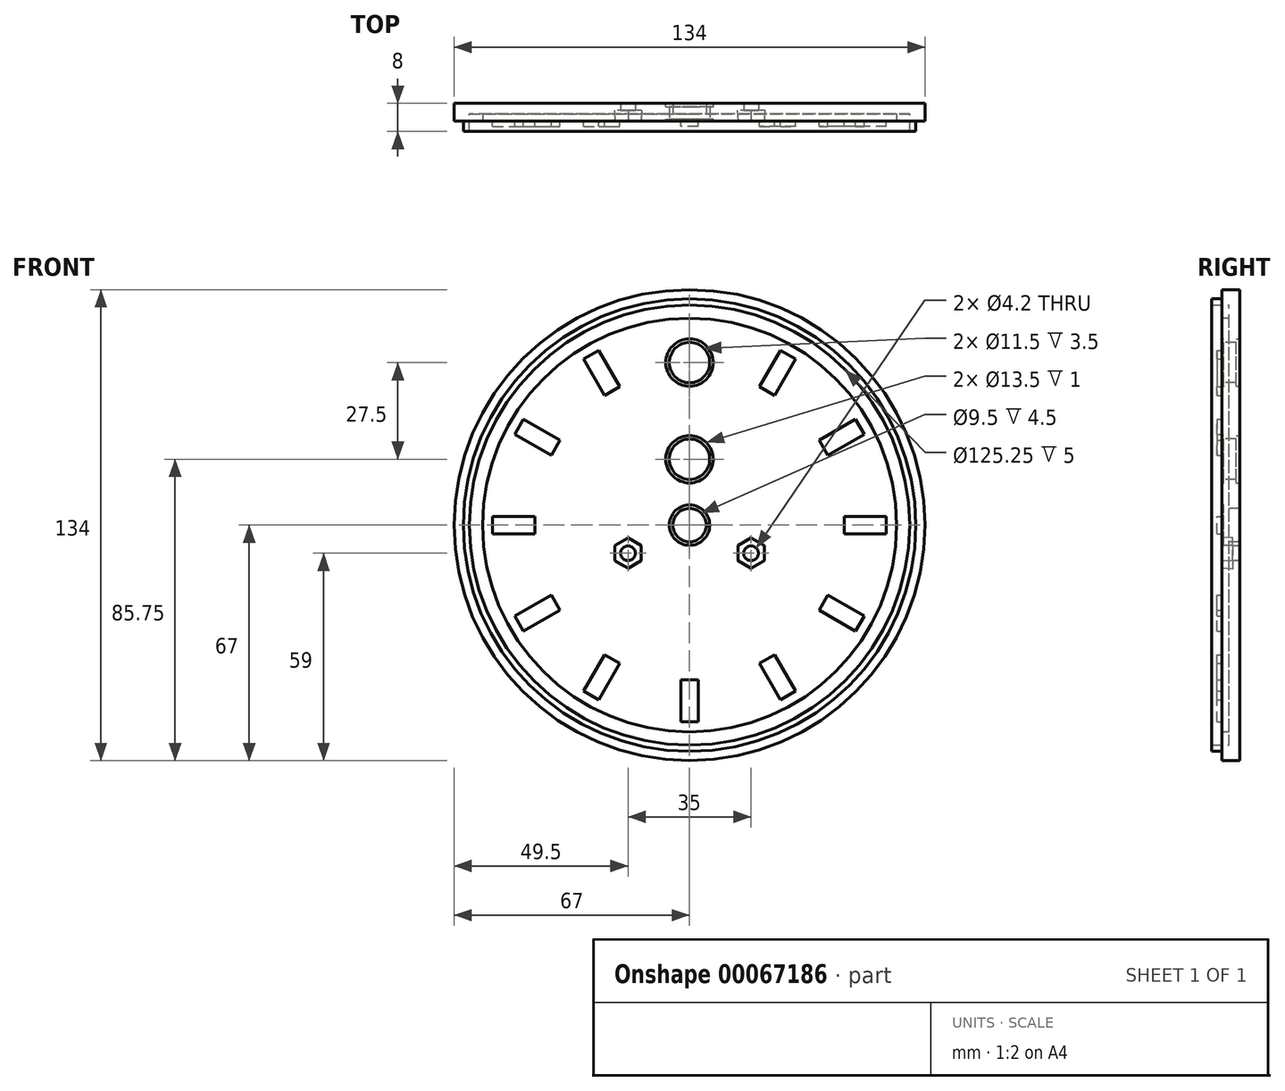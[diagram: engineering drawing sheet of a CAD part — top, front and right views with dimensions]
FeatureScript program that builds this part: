
annotation { "Feature Type Name" : "Feature", "Feature Type Description" : "" }
export const myFeature = defineFeature(function(context is Context, id is Id, definition is map)
    precondition{}
    {
        {
            var Q0;
            Q0=qCreatedBy(makeId("Front.planeOp"),FACE);
            var sketch = newSketch(context, id + "F0", { "sketchPlane" : qUnion([Q0])});
            skCircle(sketch, "E0", {"center": v(0, 0) * mm, "radius": 67 * mm});
            skSolve(sketch);
        }
        {
            var Q0;
            Q0 = qSketchRegion(id + "F0", true);
            extrude(context, id + "F1", {"entities" : qUnion([Q0]), "depth" : 5 * mm});
        }
        {
            var Q0;
            Q0=makeQuery(id+"F1.opExtrude","CAP_FACE",FACE,{"disambiguationData":[OSD([sQuery(id+"F0.wireOp",EDGE,"E0")])],"isStart":false});
            var sketch = newSketch(context, id + "F2", { "sketchPlane" : qUnion([Q0])});
            skCircle(sketch, "E1", {"center": v(0, 0) * mm, "radius": 58.88 * mm});
            skCircle(sketch, "E2", {"center": v(0, 0) * mm, "radius": 62.62 * mm});
            skCircle(sketch, "E3", {"center": v(0, 0) * mm, "radius": 64.38 * mm});
            skSolve(sketch);
        }
        {
            var Q0;
            Q0=makeQuery(id+"F2.imprint","IMPRINT",FACE,{"disambiguationData":[TD([[makeQuery(id+"F2.imprint","IMPRINT",EDGE,{"derivedFrom":sQuery(id+"F2.wireOp",EDGE,"E2")}),-1.0]])]});
            extrude(context, id + "F3", {"entities" : qUnion([Q0]), "operationType" : NewBodyOperationType.ADD, "depth" : 3 * mm});
        }
        {
            var Q0;
            Q0=makeQuery(id+"F2.imprint","IMPRINT",FACE,{"disambiguationData":[TD([[makeQuery(id+"F2.imprint","IMPRINT",EDGE,{"derivedFrom":sQuery(id+"F2.wireOp",EDGE,"E1")}),-1.0]])]});
            extrude(context, id + "F4", {"entities" : qUnion([Q0]), "operationType" : NewBodyOperationType.REMOVE, "oppositeDirection" : true, "depth" : 2 * mm});
        }
        {
            var Q0;
            Q0=makeQuery(id+"F2.imprint","IMPRINT",FACE,{"disambiguationData":[TD([[makeQuery(id+"F2.imprint","IMPRINT",EDGE,{"derivedFrom":sQuery(id+"F2.wireOp",EDGE,"E1")}),1.0]])]});
            var sketch = newSketch(context, id + "F5", { "sketchPlane" : qUnion([Q0])});
            skCircle(sketch, "E4", {"center": v(0, 0) * mm, "radius": 4.75 * mm});
            skLineSegment(sketch, "E5", {"start": v(0, 0) * mm, "end": v(0, 18.75) * mm, "construction": true});
            skCircle(sketch, "E6", {"center": v(0, 18.75) * mm, "radius": 5.75 * mm});
            skLineSegment(sketch, "E7", {"start": v(0, 18.75) * mm, "end": v(0, 46.25) * mm, "construction": true});
            skCircle(sketch, "E8", {"center": v(0, 46.25) * mm, "radius": 5.75 * mm});
            skLineSegment(sketch, "E9", {"start": v(0, 0) * mm, "end": v(0, -8) * mm, "construction": true});
            skLineSegment(sketch, "E10", {"start": v(0, -8) * mm, "end": v(17.5, -8) * mm, "construction": true});
            skCircle(sketch, "E11", {"center": v(17.5, -8) * mm, "radius": 2.1 * mm});
            skCircle(sketch, "E12.MirrorC", {"center": v(-17.5, -8) * mm, "radius": 2.1 * mm});
            skSolve(sketch);
        }
        {
            var Q0;
            Q0 = qSketchRegion(id + "F5", true);
            extrude(context, id + "F6", {"entities" : qUnion([Q0]), "operationType" : NewBodyOperationType.REMOVE, "oppositeDirection" : true, "depth" : 25 * mm});
        }
        {
            var Q0;
            Q0=makeQuery(id+"F2.imprint","IMPRINT",FACE,{"disambiguationData":[TD([[makeQuery(id+"F2.imprint","IMPRINT",EDGE,{"derivedFrom":sQuery(id+"F2.wireOp",EDGE,"E1")}),1.0]])]});
            var sketch = newSketch(context, id + "F7", { "sketchPlane" : qUnion([Q0])});
            skCircle(sketch, "E13", {"center": v(0, 0) * mm, "radius": 5.75 * mm});
            skCircle(sketch, "E14", {"center": v(0, 18.75) * mm, "radius": 6.75 * mm});
            skCircle(sketch, "E15", {"center": v(0, 46.25) * mm, "radius": 6.75 * mm});
            skSolve(sketch);
        }
        {
            var Q0;
            Q0 = qSketchRegion(id + "F7", true);
            extrude(context, id + "F8", {"entities" : qUnion([Q0]), "operationType" : NewBodyOperationType.REMOVE, "oppositeDirection" : true, "depth" : .5 * mm, "hasDraft" : true, "draftAngle" : 3 * degree});
        }
        {
            var Q0;
            Q0=makeQuery(id+"F2.imprint","IMPRINT",FACE,{"disambiguationData":[TD([[makeQuery(id+"F2.imprint","IMPRINT",EDGE,{"derivedFrom":sQuery(id+"F2.wireOp",EDGE,"E1")}),1.0]])]});
            var sketch = newSketch(context, id + "F9", { "sketchPlane" : qUnion([Q0])});
            skCircle(sketch, "E16.cCircle", {"center": v(17.5, -8) * mm, "radius": 3.75 * mm, "construction": true});
            skLineSegment(sketch, "E16.0", {"start": v(21.25, -5.83) * mm, "end": v(21.25, -10.17) * mm});
            skLineSegment(sketch, "E16.1", {"start": v(21.25, -10.17) * mm, "end": v(17.5, -12.33) * mm});
            skLineSegment(sketch, "E16.2", {"start": v(17.5, -12.33) * mm, "end": v(13.75, -10.17) * mm});
            skLineSegment(sketch, "E16.3", {"start": v(13.75, -10.17) * mm, "end": v(13.75, -5.83) * mm});
            skLineSegment(sketch, "E16.4", {"start": v(13.75, -5.83) * mm, "end": v(17.5, -3.67) * mm});
            skLineSegment(sketch, "E16.5", {"start": v(17.5, -3.67) * mm, "end": v(21.25, -5.83) * mm});
            skPoint(sketch, "E16.0.midPoint", {"position": v(21.25, -8) * mm});
            skLineSegment(sketch, "E17.MirrorCS", {"start": v(-21.25, -5.83) * mm, "end": v(-21.25, -10.17) * mm});
            skLineSegment(sketch, "E18.MirrorCS", {"start": v(-13.75, -5.83) * mm, "end": v(-17.5, -3.67) * mm});
            skLineSegment(sketch, "E19.MirrorCS", {"start": v(-17.5, -3.67) * mm, "end": v(-21.25, -5.83) * mm});
            skCircle(sketch, "E20.MirrorC", {"center": v(-17.5, -8) * mm, "radius": 3.75 * mm, "construction": true});
            skPoint(sketch, "E21.MirrorP", {"position": v(-21.25, -8) * mm});
            skLineSegment(sketch, "E22.MirrorCS", {"start": v(-21.25, -10.17) * mm, "end": v(-17.5, -12.33) * mm});
            skLineSegment(sketch, "E23.MirrorCS", {"start": v(-17.5, -12.33) * mm, "end": v(-13.75, -10.17) * mm});
            skLineSegment(sketch, "E24.MirrorCS", {"start": v(-13.75, -10.17) * mm, "end": v(-13.75, -5.83) * mm});
            skSolve(sketch);
        }
        {
            var Q0;
            Q0 = qSketchRegion(id + "F9", true);
            extrude(context, id + "F10", {"entities" : qUnion([Q0]), "operationType" : NewBodyOperationType.REMOVE, "oppositeDirection" : true, "depth" : 3 * mm, "hasDraft" : true, "draftAngle" : 3 * degree});
        }
        {
            var Q0;
            Q0=qCreatedBy(makeId("Front.planeOp"),FACE);
            var sketch = newSketch(context, id + "F11", { "sketchPlane" : qUnion([Q0])});
            skCircle(sketch, "E25.0", {"center": v(0, 46.25) * mm, "radius": 6.75 * mm});
            skCircle(sketch, "E25.1", {"center": v(0, 18.75) * mm, "radius": 6.75 * mm});
            skSolve(sketch);
        }
        {
            var Q0;
            Q0 = qSketchRegion(id + "F11", true);
            extrude(context, id + "F12", {"entities" : qUnion([Q0]), "operationType" : NewBodyOperationType.REMOVE, "depth" : 1 * mm});
        }
        {
            var Q0;
            Q0=makeQuery(id+"F7.imprint","IMPRINT",FACE,{"disambiguationData":[TD([[makeQuery(id+"F7.imprint","IMPRINT",EDGE,{"derivedFrom":sQuery(id+"F7.wireOp",EDGE,"E13")}),-1.0]])]});
            var sketch = newSketch(context, id + "F13", { "sketchPlane" : qUnion([Q0])});
            skCircle(sketch, "E26", {"center": v(0, 0) * mm, "radius": 50 * mm, "construction": true});
            skPoint(sketch, "E27", {"position": v(0, -50) * mm});
            skLineSegment(sketch, "E28.rect.bottom", {"start": v(2.5, -56) * mm, "end": v(-2.5, -56) * mm});
            skLineSegment(sketch, "E28.rect.top", {"start": v(2.5, -44) * mm, "end": v(-2.5, -44) * mm});
            skLineSegment(sketch, "E28.rect.left", {"start": v(2.5, -56) * mm, "end": v(2.5, -44) * mm});
            skLineSegment(sketch, "E28.rect.right", {"start": v(-2.5, -56) * mm, "end": v(-2.5, -44) * mm});
            skLineSegment(sketch, "E29", {"start": v(0, -66.73) * mm, "end": v(0, 0) * mm, "construction": true});
            skSolve(sketch);
        }
        {
            var Q0;
            Q0 = qSketchRegion(id + "F13", true);
            extrude(context, id + "F14", {"entities" : qUnion([Q0]), "operationType" : NewBodyOperationType.ADD, "depth" : 1.5 * mm});
        }
        {
            var Q0;
            Q0=makeQuery(id+"F14.opExtrude","SWEPT_FACE",FACE,{"disambiguationData":[OSD([sQuery(id+"F13.wireOp",EDGE,"E28.rect.right")])]});
            var Q1;
            Q1=makeQuery(id+"F14.opExtrude","SWEPT_FACE",FACE,{"disambiguationData":[OSD([sQuery(id+"F13.wireOp",EDGE,"E28.rect.top")])]});
            var Q2;
            Q2=makeQuery(id+"F14.opExtrude","CAP_FACE",FACE,{"disambiguationData":[OSD([sQuery(id+"F13.wireOp",EDGE,"E28.rect.bottom"),sQuery(id+"F13.wireOp",EDGE,"E28.rect.top"),sQuery(id+"F13.wireOp",EDGE,"E28.rect.left"),sQuery(id+"F13.wireOp",EDGE,"E28.rect.right")])],"isStart":false});
            var Q3;
            Q3=makeQuery(id+"F14.opExtrude","SWEPT_FACE",FACE,{"disambiguationData":[OSD([sQuery(id+"F13.wireOp",EDGE,"E28.rect.bottom")])]});
            var Q4;
            Q4=makeQuery(id+"F14.opExtrude","SWEPT_FACE",FACE,{"disambiguationData":[OSD([sQuery(id+"F13.wireOp",EDGE,"E28.rect.left")])]});
            var Q5;
            Q5=sQuery(id+"F13.wireOp",EDGE,"E26");
            circularPattern(context, id + "F15", {"faces" : qUnion([Q0, Q1, Q2, Q3, Q4]), "axis" : qUnion([Q5]), "angle" : 30 * degree, "instanceCount" : 6, "patternType" : PatternType.FACE});
        }
        {
            var Q0;
            Q0=makeQuery(id+"F14.opExtrude","SWEPT_FACE",FACE,{"disambiguationData":[OSD([sQuery(id+"F13.wireOp",EDGE,"E28.rect.right")])]});
            var Q1;
            Q1=makeQuery(id+"F14.opExtrude","CAP_FACE",FACE,{"disambiguationData":[OSD([sQuery(id+"F13.wireOp",EDGE,"E28.rect.bottom"),sQuery(id+"F13.wireOp",EDGE,"E28.rect.top"),sQuery(id+"F13.wireOp",EDGE,"E28.rect.left"),sQuery(id+"F13.wireOp",EDGE,"E28.rect.right")])],"isStart":false});
            var Q2;
            Q2=makeQuery(id+"F14.opExtrude","SWEPT_FACE",FACE,{"disambiguationData":[OSD([sQuery(id+"F13.wireOp",EDGE,"E28.rect.top")])]});
            var Q3;
            Q3=makeQuery(id+"F14.opExtrude","SWEPT_FACE",FACE,{"disambiguationData":[OSD([sQuery(id+"F13.wireOp",EDGE,"E28.rect.left")])]});
            var Q4;
            Q4=makeQuery(id+"F14.opExtrude","SWEPT_FACE",FACE,{"disambiguationData":[OSD([sQuery(id+"F13.wireOp",EDGE,"E28.rect.bottom")])]});
            var Q5;
            Q5=sQuery(id+"F13.wireOp",EDGE,"E26");
            circularPattern(context, id + "F16", {"faces" : qUnion([Q0, Q1, Q2, Q3, Q4]), "axis" : qUnion([Q5]), "angle" : 30 * degree, "instanceCount" : 6, "oppositeDirection" : true, "patternType" : PatternType.FACE});
        }
    });
